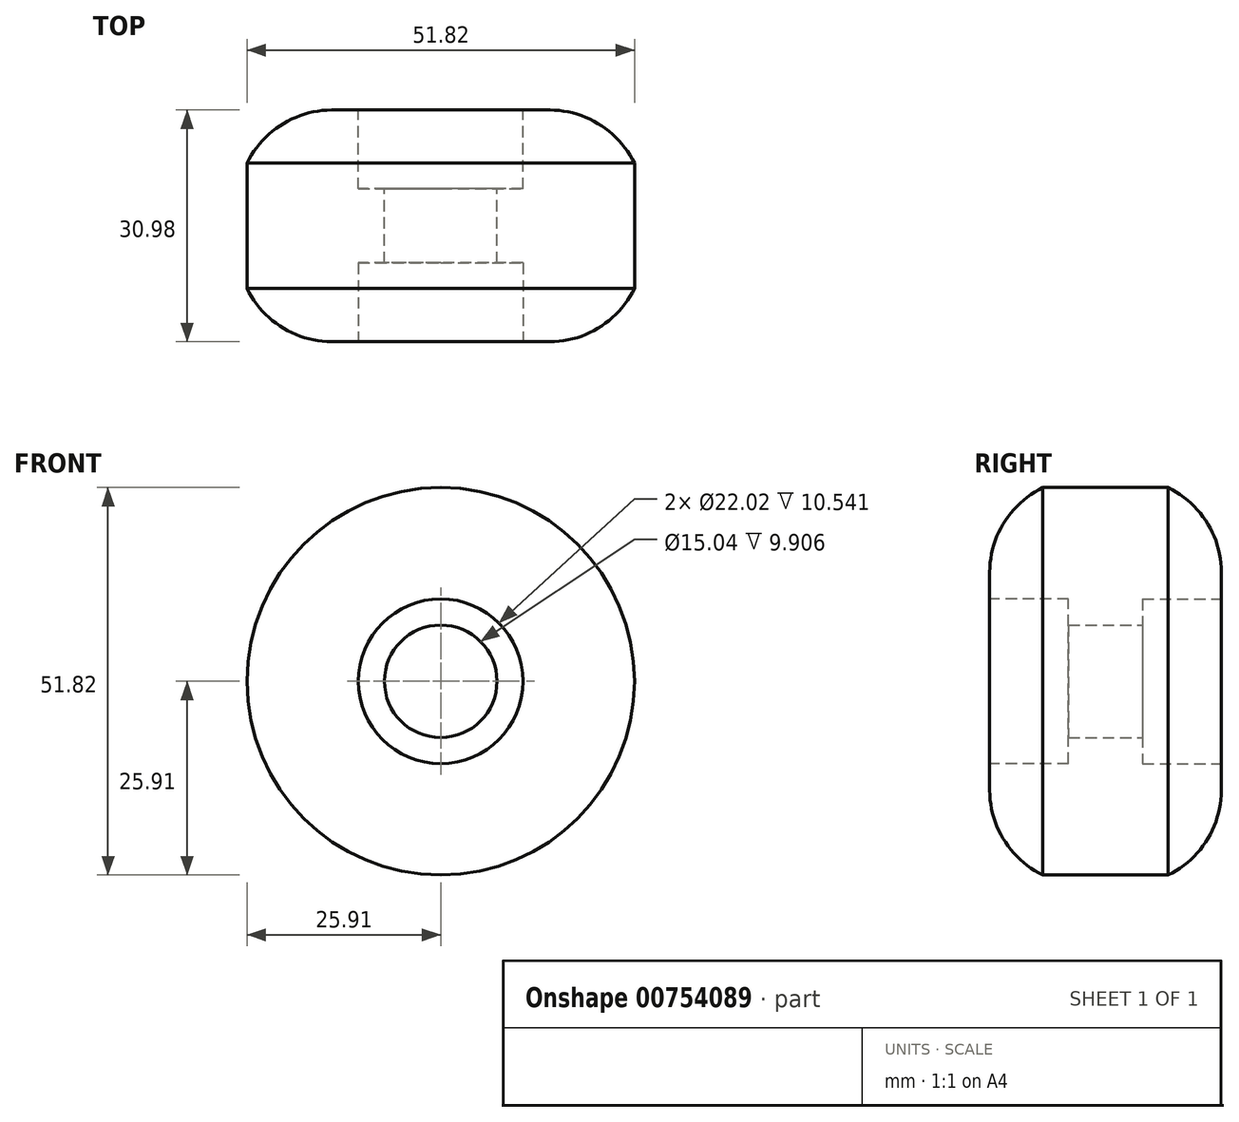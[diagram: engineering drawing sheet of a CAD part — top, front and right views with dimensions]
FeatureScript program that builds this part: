
annotation { "Feature Type Name" : "Feature", "Feature Type Description" : "" }
export const myFeature = defineFeature(function(context is Context, id is Id, definition is map)
    precondition{}
    {
        {
            var Q0;
            Q0=qCreatedBy(makeId("Front.planeOp"),FACE);
            var sketch = newSketch(context, id + "F0", { "sketchPlane" : qUnion([Q0])});
            skCircle(sketch, "E0", {"center": v(0, 0) * mm, "radius": 7.52 * mm});
            skCircle(sketch, "E1", {"center": v(0, 0) * mm, "radius": 25.9 * mm});
            skSolve(sketch);
        }
        {
            var Q0;
            Q0 = qSketchRegion(id + "F0", true);
            extrude(context, id + "F1", {"entities" : qUnion([Q0]), "depth" : 30.99 * mm, "offsetDistance" : 25.4 * mm, "symmetric" : true});
        }
        {
            var Q0;
            Q0=makeQuery(id+"F1.opExtrude","CAP_FACE",FACE,{"disambiguationData":[OSD([sQuery(id+"F0.wireOp",EDGE,"E0"),sQuery(id+"F0.wireOp",EDGE,"E1")])],"isStart":false});
            var sketch = newSketch(context, id + "F2", { "sketchPlane" : qUnion([Q0])});
            skCircle(sketch, "E2", {"center": v(0, 0) * mm, "radius": 11.01 * mm});
            skSolve(sketch);
        }
        {
            var Q0;
            Q0 = qSketchRegion(id + "F2", true);
            extrude(context, id + "F3", {"entities" : qUnion([Q0]), "operationType" : NewBodyOperationType.REMOVE, "oppositeDirection" : true, "depth" : 10.54 * mm, "offsetDistance" : 25.4 * mm});
        }
        {
            var Q0;
            Q0=makeQuery(id+"F1.opExtrude","CAP_FACE",FACE,{"disambiguationData":[OSD([sQuery(id+"F0.wireOp",EDGE,"E0"),sQuery(id+"F0.wireOp",EDGE,"E1")])],"isStart":true});
            var sketch = newSketch(context, id + "F4", { "sketchPlane" : qUnion([Q0])});
            skCircle(sketch, "E3", {"center": v(0, 0) * mm, "radius": 11.01 * mm});
            skSolve(sketch);
        }
        {
            var Q0;
            Q0 = qSketchRegion(id + "F4", true);
            extrude(context, id + "F5", {"entities" : qUnion([Q0]), "operationType" : NewBodyOperationType.REMOVE, "oppositeDirection" : true, "depth" : 10.54 * mm, "offsetDistance" : 25.4 * mm});
        }
        {
            var Q0;
            Q0=qCreatedBy(makeId("Right.planeOp"),FACE);
            var sketch = newSketch(context, id + "F6", { "sketchPlane" : qUnion([Q0])});
            skLineSegment(sketch, "E4.bottom", {"start": v(8.38, 25.9) * mm, "end": v(-8.38, 25.9) * mm});
            skPoint(sketch, "E4.middle", {"position": v(0, 0) * mm});
            skLineSegment(sketch, "E5.left", {"start": v(15.5, 14.6) * mm, "end": v(15.5, 14.4) * mm});
            skLineSegment(sketch, "E5.right", {"start": v(-15.5, 14.6) * mm, "end": v(-15.5, 14.4) * mm});
            skArc(sketch, "E6", {"start": v(0, 26.9) * mm, "mid": v(-10.77, 24.4) * mm, "end": v(-15.5, 14.4) * mm});
            skPoint(sketch, "E6.second.point", {"position": v(-13.28, 21.66) * mm});
            skPoint(sketch, "E6.third.point", {"position": v(-15.5, 14.6) * mm});
            skArc(sketch, "E7.MirrorC", {"start": v(0, 26.9) * mm, "mid": v(10.77, 24.4) * mm, "end": v(15.5, 14.4) * mm});
            skLineSegment(sketch, "E8.top", {"start": v(-15.5, 30.48) * mm, "end": v(15.5, 30.48) * mm});
            skLineSegment(sketch, "E8.left", {"start": v(-15.5, 14.6) * mm, "end": v(-15.5, 30.48) * mm});
            skLineSegment(sketch, "E8.right", {"start": v(15.5, 14.6) * mm, "end": v(15.5, 30.48) * mm});
            skPoint(sketch, "E5.top.start.orphan", {"position": v(15.5, -14.6) * mm});
            skPoint(sketch, "E9.trimOffspring.end.orphan", {"position": v(-15.5, -14.6) * mm});
            skPoint(sketch, "E4.left.end.orphan", {"position": v(8.38, -25.9) * mm});
            skPoint(sketch, "E4.right.end.orphan", {"position": v(-8.38, -25.9) * mm});
            skSolve(sketch);
        }
        {
            var Q0;
            Q0 = qSketchRegion(id + "F6", true);
            var Q1;
            Q1=makeQuery(id+"F3.boolean.opBoolean","INTERSECT",EDGE,{"derivedFrom":[makeQuery(id+"F1.opExtrude","SWEPT_FACE",FACE,{"disambiguationData":[OSD([sQuery(id+"F0.wireOp",EDGE,"E0")])]}),makeQuery(id+"F3.opExtrude","CAP_FACE",FACE,{"disambiguationData":[OSD([sQuery(id+"F2.wireOp",EDGE,"E2")])],"isStart":false})]});
            revolve(context, id + "F7", {"operationType" : NewBodyOperationType.REMOVE, "surfaceOperationType" : NewSurfaceOperationType.NEW, "entities" : qUnion([Q0]), "axis" : qUnion([Q1]), "revolveType" : RevolveType.FULL, "oppositeDirection" : true});
        }
    });
